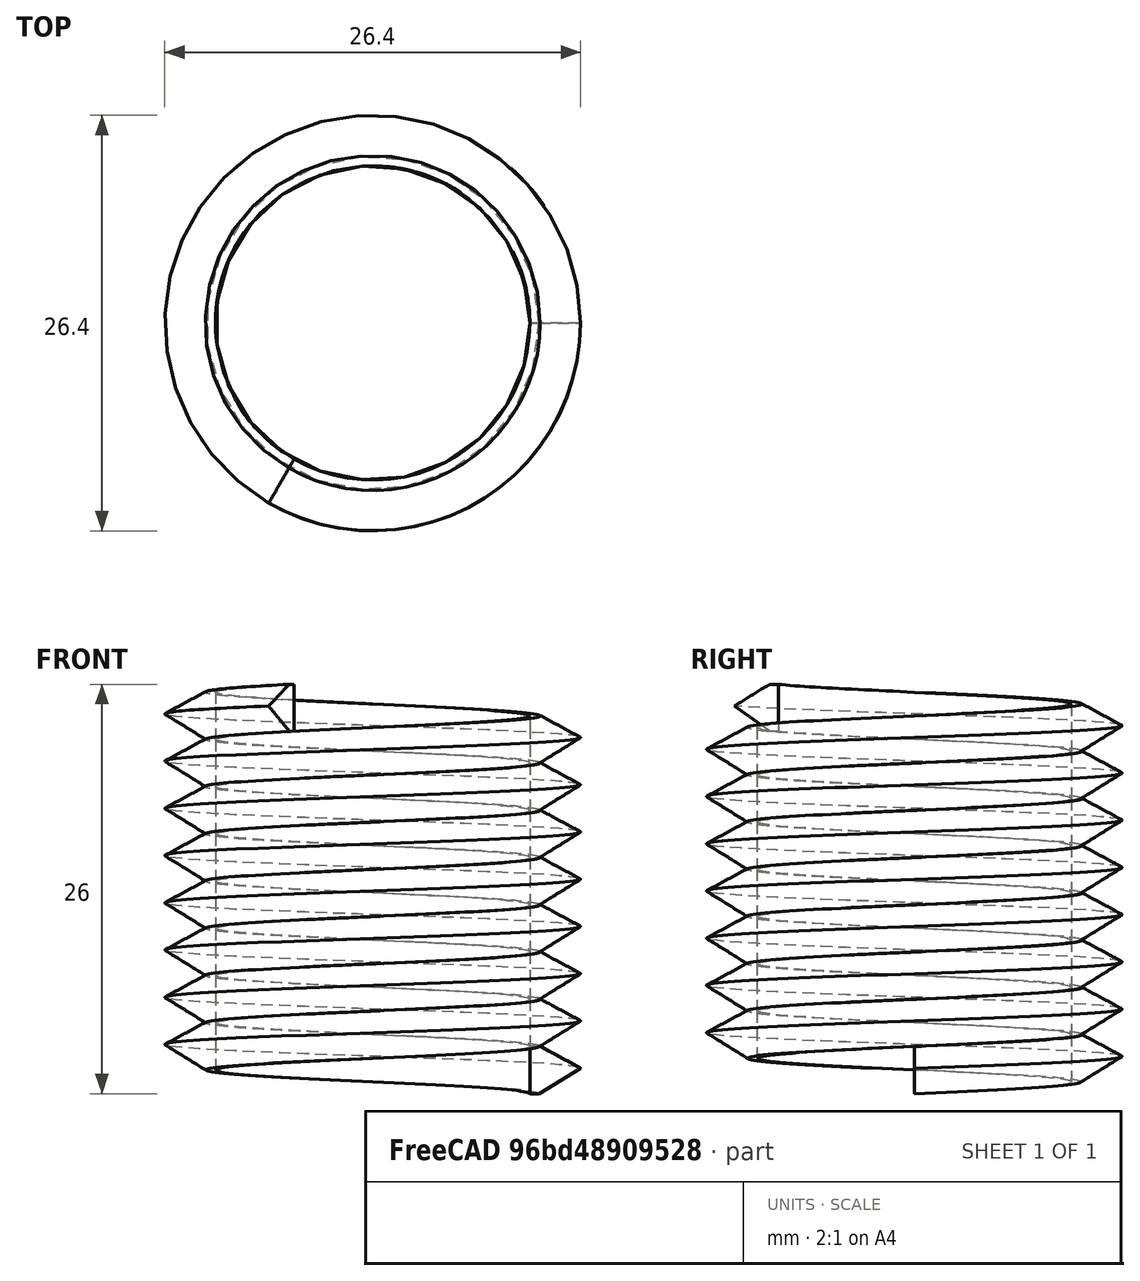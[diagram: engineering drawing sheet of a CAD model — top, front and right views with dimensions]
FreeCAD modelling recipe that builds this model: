
FCSTD DOCUMENT  (FreeCAD 0.18.4R)
Label: helical_coil
License: All rights reserved
LicenseURL: http://en.wikipedia.org/wiki/All_rights_reserved
objects: Sketcher::SketchObject×2, Part::Helix×1, PartDesign::AdditivePipe×1, PartDesign::Body×1
note: 6 computed .brp shape members not serialized (recipe doc carries the construction recipe); baked Part::Feature solids carry a one-line shape summary decoded from their .brp

FEATURE [Part::Helix] Helix
  Angle = 0
  AttacherType = Attacher::AttachEngine3D
  Height = 23
  LocalCoord = 0
  Pitch = 3
  Radius = 10
  Style = 1
  expr: Radius = 10
FEATURE [Sketcher::SketchObject] Sketch
  ExternalGeometry = -> [Helix]
  MapMode = 7
  Placement = pos=(10,2.1e-15,0) rot=(1,0,0;1.61851rad)
  Support = -> [Helix]
  sketch-geometry (4):
    g0: LineSegment StartX=-0.09109 StartY=0.152018 StartZ=0 EndX=1.38456 EndY=0.230786 EndZ=0
    g1: LineSegment StartX=1.38315 StartY=0.871232 StartZ=0 EndX=1.8e-15 EndY=2.99659 EndZ=0
    g2: LineSegment StartX=1.8e-15 StartY=2.99659 StartZ=0 EndX=-0.09109 EndY=0.152018 EndZ=0
    g3: ArcOfCircle CenterX=0.765339 CenterY=0.549645 CenterZ=0 NormalX=0 NormalY=0 NormalZ=1 AngleXU=0 Radius=0.696495 StartAngle=5.80766 EndAngle=6.76312
  constraints (6):
    c: Coincident(g1,g-3)
    c: Coincident(g2,g1)
    c: Coincident(g0,g2)
    c: Coincident(g1,g3)
    c: Coincident(g3,g0)
    c: Angle(g1,g0) = 1.0472
FEATURE [Sketcher::SketchObject] Sketch001
  MapMode = 5
  Placement = pos=(0,0,0) rot=(1,0,0;1.5708rad)
  Support = -> [XZ_Plane]
  sketch-geometry (5):
    g0: LineSegment StartX=9.97859 StartY=-0.011025 StartZ=0 EndX=10.5734 EndY=-0.011025 EndZ=0
    g1: LineSegment StartX=10.5734 StartY=-0.011025 StartZ=0 EndX=13.1959 EndY=1.61227 EndZ=0
    g2: LineSegment StartX=13.1959 StartY=1.61227 StartZ=0 EndX=10.6353 EndY=2.98773 EndZ=0
    g3: LineSegment StartX=10.6353 StartY=2.98773 StartZ=0 EndX=9.97859 EndY=2.98773 EndZ=0
    g4: LineSegment StartX=9.97859 StartY=2.98773 StartZ=0 EndX=9.97859 EndY=-0.011025 EndZ=0
  constraints (9):
    c: Coincident(g0,g1)
    c: Coincident(g1,g2)
    c: Coincident(g2,g3)
    c: Coincident(g3,g4)
    c: Coincident(g4,g0)
    c: Vertical(g4)
    c: Horizontal(g3)
    c: Horizontal(g0)
    c: Angle(g2,g1) = 1.0472
FEATURE [PartDesign::AdditivePipe] AdditivePipe
  AuxilleryCurvelinear = true
  AuxillerySpineTangent = false
  Binormal = (0,0,0)
  Mode = 2
  Placement = pos=(0,0,0) rot=(1,0,0;1.5708rad)
  Profile = -> Sketch001
  Spine = -> Helix
  SpineTangent = false
  Transformation = 0
  Transition = 0
FEATURE [PartDesign::Body] Body
  Group = -> [Sketch001,AdditivePipe]
  Origin = -> Origin
  Tip = -> AdditivePipe
